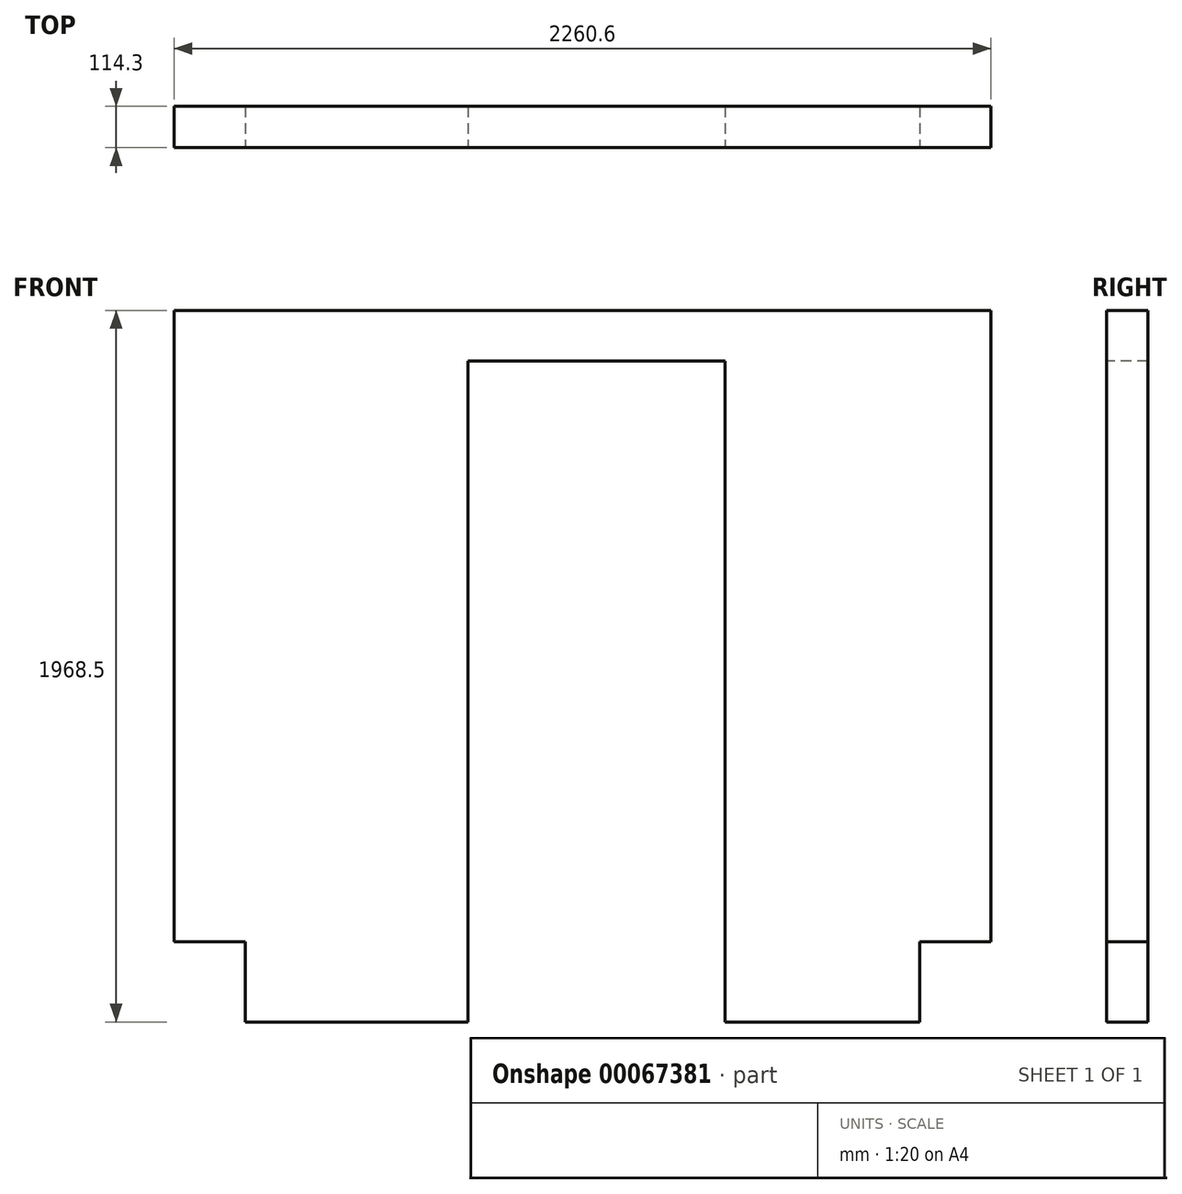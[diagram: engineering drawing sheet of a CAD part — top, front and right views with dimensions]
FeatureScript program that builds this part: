
annotation { "Feature Type Name" : "Feature", "Feature Type Description" : "" }
export const myFeature = defineFeature(function(context is Context, id is Id, definition is map)
    precondition{}
    {
        {
            var Q0;
            Q0=qCreatedBy(makeId("Top.planeOp"),FACE);
            var sketch = newSketch(context, id + "F0", { "sketchPlane" : qUnion([Q0])});
            skLineSegment(sketch, "E0", {"start": v(0, -1028.7) * mm, "end": v(0, -914.4) * mm});
            skLineSegment(sketch, "E1", {"start": v(-2260.6, -1028.7) * mm, "end": v(0, -1028.7) * mm});
            skLineSegment(sketch, "E2", {"start": v(-2260.6, -1028.7) * mm, "end": v(-2260.6, -914.4) * mm});
            skLineSegment(sketch, "E3", {"start": v(-2260.6, -914.4) * mm, "end": v(0, -914.4) * mm});
            skSolve(sketch);
        }
        {
            var Q0;
            Q0 = qSketchRegion(id + "F0", true);
            extrude(context, id + "F1", {"entities" : qUnion([Q0]), "depth" : 1968.5 * mm});
        }
        {
            var Q0;
            Q0=makeQuery(id+"F1.opExtrude","SWEPT_FACE",FACE,{"disambiguationData":[OSD([sQuery(id+"F0.wireOp",EDGE,"E1")])]});
            var sketch = newSketch(context, id + "F2", { "sketchPlane" : qUnion([Q0])});
            skLineSegment(sketch, "E4.bottom", {"start": v(-1447.8, 0) * mm, "end": v(-736.6, 0) * mm});
            skLineSegment(sketch, "E4.top", {"start": v(-1447.8, 1828.8) * mm, "end": v(-736.6, 1828.8) * mm});
            skLineSegment(sketch, "E4.left", {"start": v(-1447.8, 0) * mm, "end": v(-1447.8, 1828.8) * mm});
            skLineSegment(sketch, "E4.right", {"start": v(-736.6, 0) * mm, "end": v(-736.6, 1828.8) * mm});
            skSolve(sketch);
        }
        {
            var Q0;
            Q0 = qSketchRegion(id + "F2", true);
            extrude(context, id + "F3", {"entities" : qUnion([Q0]), "operationType" : NewBodyOperationType.REMOVE, "endBound" : BoundingType.THROUGH_ALL, "oppositeDirection" : true, "depth" : 25.4 * mm});
        }
        {
            var Q0;
            Q0=makeQuery(id+"F1.opExtrude","SWEPT_FACE",FACE,{"disambiguationData":[OSD([sQuery(id+"F0.wireOp",EDGE,"E1")])]});
            var sketch = newSketch(context, id + "F4", { "sketchPlane" : qUnion([Q0])});
            skLineSegment(sketch, "E5.bottom", {"start": v(-2260.6, 0) * mm, "end": v(-2063.75, 0) * mm});
            skLineSegment(sketch, "E5.top", {"start": v(-2260.6, 222.25) * mm, "end": v(-2063.75, 222.25) * mm});
            skLineSegment(sketch, "E5.left", {"start": v(-2260.6, 0) * mm, "end": v(-2260.6, 222.25) * mm});
            skLineSegment(sketch, "E5.right", {"start": v(-2063.75, 0) * mm, "end": v(-2063.75, 222.25) * mm});
            skLineSegment(sketch, "E6.bottom", {"start": v(0, 0) * mm, "end": v(-196.85, 0) * mm});
            skLineSegment(sketch, "E6.top", {"start": v(0, 222.25) * mm, "end": v(-196.85, 222.25) * mm});
            skLineSegment(sketch, "E6.left", {"start": v(0, 0) * mm, "end": v(0, 222.25) * mm});
            skLineSegment(sketch, "E6.right", {"start": v(-196.85, 0) * mm, "end": v(-196.85, 222.25) * mm});
            skSolve(sketch);
        }
        {
            var Q0;
            Q0 = qSketchRegion(id + "F4", true);
            extrude(context, id + "F5", {"entities" : qUnion([Q0]), "operationType" : NewBodyOperationType.REMOVE, "endBound" : BoundingType.THROUGH_ALL, "oppositeDirection" : true, "depth" : 25.4 * mm});
        }
    });
